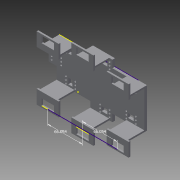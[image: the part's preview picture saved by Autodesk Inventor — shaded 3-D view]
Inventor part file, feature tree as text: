
AUTODESK INVENTOR PART (.ipt)
format: ipt  version: 2015 (Build 190159000, 159)  size: 573,952 bytes
history: native  units: mm
features: sketch x31, extrude x23, pattern_linear x1
ambient origin geometry x8: Origin, YZ Plane, XZ Plane, XY Plane, X Axis, Y Axis, Z Axis, Center Point
bodies: Solid1 (feature_tree)
feature tree (55):
  extrude  "Extrusion1"  Depth=75.0mm
  sketch  "Sketch2"  dims[d2=5.0mm d3=0.0mm d4=50.0mm]
  sketch  "Sketch3"  dims[d5=50.0mm d6=50.0mm]
  extrude  "Extrusion3"  Depth=50.0mm
  extrude  "Extrusion4"  Depth=50.0mm
  extrude  "Extrusion5"  Depth=24.0mm
  extrude  "Extrusion6"  Depth=24.0mm
  extrude  "Extrusion7"  Depth=6.0mm
  extrude  "Extrusion8"  Depth=8.0mm
  sketch  "Sketch14"  dims[d23=4.25mm d24=4.25mm]
  extrude  "Extrusion13"  Depth=4.25mm
  sketch  "Sketch16"  dims[d27=4.25mm d28=4.25mm]
  sketch  "Sketch18"  dims[d29=4.25mm d30=6.0mm]
  extrude  "Extrusion14"  Depth=6.0mm
  extrude  "Extrusion16"  Depth=4.25mm
  extrude  "Extrusion17"  Depth=6.0mm
  extrude  "Extrusion18"  Depth=4.25mm
  extrude  "Extrusion19"  Depth=6.0mm
  extrude  "Extrusion20"  Depth=6.0mm
  sketch  "Sketch27"  dims[d46=34.05mm d47=0.0mm d48=4.0mm]
  sketch  "Sketch28"  dims[d49=3.0mm d50=4.0mm]
  extrude  "Extrusion21"  Depth=6.0mm
  extrude  "Extrusion22"  Depth=4.25mm
  extrude  "Extrusion23"  Depth=4.25mm
  extrude  "Extrusion24"  Depth=34.0mm
  extrude  "Extrusion25"  Depth=3.0mm
  extrude  "Extrusion26"  Depth=4.0mm
  extrude  "Extrusion27"  Depth=4.0mm
  sketch  "Sketch35"  dims[d60=23.0mm d61=0.0mm]
  extrude  "Extrusion28"  Depth=4.0mm
  pattern_linear  "Rectangular Pattern1"  Spacing1=6.0mm  [1 undecoded]
  extrude  "Extrusion29"  Depth=6.0mm
  sketch  "Sketch38"  dims[d64=18.0mm d65=6.0mm d66=6.0mm d67=4.25mm d68=4.25mm d69=4.25mm d70=4.25mm d71=4.25mm d72=6.0mm d73=4.25mm d74=18.0mm d75=6.0mm d76=6.0mm d77=4.25mm d78=4.25mm d79=4.25mm d80=4.25mm d81=4.25mm d82=20.0mm d83=0.0mm d84=11.0mm d85=11.0mm d86=2.25mm d87=2.25mm d88=3.0mm d89=2.25mm d90=2.25mm d91=3.0mm d92=20.0mm d93=0.0mm d108=9.0mm d109=8.0mm d110=11.0mm d111=8.0mm d112=11.0mm d113=26.0mm d114=0.0mm d115=23.5mm d116=23.5mm d117=36.0mm d118=24.0mm d119=36.0mm d120=24.0mm d121=14.0mm d122=14.0mm d123=5.0mm d124=0.0mm d125=6.0mm d126=9.0mm d127=18.0mm d130=6.0mm d135=6.0mm d136=6.0mm d153=3.0mm d154=3.0mm d155=34.05mm d156=0.0mm d157=4.0mm d158=42.0mm d159=26.0mm d160=26.0mm d161=3.0mm d162=0.0mm d164=4.25mm d165=4.25mm d166=4.25mm d167=4.25mm d168=4.25mm d169=6.0mm d170=6.0mm d171=5.0mm d172=0.0mm d173=4.25mm d174=4.25mm d175=4.25mm d176=4.25mm d177=4.25mm d178=4.25mm d179=11.0mm d180=8.0mm d181=11.0mm d182=8.0mm d183=5.0mm d184=0.0mm d185=3.0mm d186=3.0mm d187=12.0mm d188=12.0mm d189=23.5mm d190=23.5mm d191=5.0mm d192=0.0mm d193=66.053538mm d194=66.054mm d195=4.25mm d196=18.0mm d197=4.25mm d198=6.0mm d199=6.0mm d200=4.25mm d201=4.25mm d202=4.25mm d203=4.25mm d204=4.25mm d205=6.0mm d206=6.0mm d207=4.25mm d208=4.25mm d209=4.25mm d210=4.25mm d211=4.25mm d212=11.0mm d213=8.0mm d214=11.0mm d215=8.0mm d216=5.0mm d217=0.0mm d218=5.0mm d219=0.0mm d220=17.0mm d221=3.0mm d222=17.0mm d223=3.0mm d224=34.05mm d225=0.0mm d226=4.0mm d227=42.0mm d228=26.0mm d229=42.0mm d230=26.0mm d231=3.0mm d232=0.0mm d233=3.0mm d234=12.0mm d235=3.0mm d236=12.0mm d237=23.5mm d238=23.5mm d239=3.0mm d240=0.0mm d241=12.0mm d242=0.0mm d244=24.0mm d245=36.0mm d246=0.0mm d247=9.0mm d248=4.25mm d249=36.0mm d250=0.0mm d251=30.0mm d253=6.0mm d254=20.0mm d256=18.0mm d257=5.0mm d258=36.0mm d259=0.0mm]
  sketch  "Sketch1"  dims[d0=150.0mm d1=75.0mm]
  sketch  "Sketch4"  dims[d7=36.0mm d8=24.0mm]
  sketch  "Sketch5"  dims[d10=36.0mm d11=24.0mm]
  sketch  "Sketch6"  dims[d12=6.0mm d13=6.0mm]
  sketch  "Sketch7"  dims[d17=8.0mm d18=4.25mm]
  sketch  "Sketch9"  dims[d19=18.0mm d20=4.25mm]
  sketch  "Sketch10"  dims[d21=6.0mm d22=6.0mm]
  sketch  "Sketch15"  dims[d25=6.0mm d26=6.0mm]
  sketch  "Sketch19"  dims[d31=6.0mm d32=18.0mm]
  sketch  "Sketch20"  dims[d33=6.0mm d34=6.0mm]
  sketch  "Sketch21"  dims[d35=4.25mm d36=4.25mm]
  sketch  "Sketch23"  dims[d37=4.25mm d38=4.25mm]
  sketch  "Sketch24"  dims[d39=4.25mm d42=34.0mm]
  sketch  "Sketch25"  dims[d43=3.0mm d45=3.0mm]
  sketch  "Sketch29"  dims[d51=3.0mm d52=4.0mm]
  sketch  "Sketch30"  dims[d53=3.0mm]
  sketch  "Sketch31"  dims[d54=4.0mm]
  sketch  "Sketch32"  dims[d55=3.0mm]
  sketch  "Sketch33"  dims[d56=3.0mm d57=0.0mm]
  sketch  "Sketch34"  dims[d58=23.0mm d59=0.0mm]
  sketch  "Sketch36"  dims[d62=6.0mm]
  sketch  "Sketch37"  dims[d63=4.25mm]
note: 1 required parameter value undecoded (feature->parameter linkage not recoverable at this tier; creation-order binding heuristic only, values carry confidence <= 0.55)
